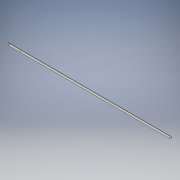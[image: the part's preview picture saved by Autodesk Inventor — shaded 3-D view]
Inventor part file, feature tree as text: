
AUTODESK INVENTOR PART (.ipt)
format: ipt  version: 2017 (Build 210142000, 142)  size: 114,688 bytes
history: native  units: in
note: dims shown in document units (in); Inventor stores cm internally (conversion verified against a paired STEP export)
features: extrude x3, sketch x3
ambient origin geometry x8: Origin, YZ Plane, XZ Plane, XY Plane, X Axis, Y Axis, Z Axis, Center Point
bodies: Solid1 (feature_tree)
feature tree (6):
  extrude  "Extrusion1"  Depth=0.128in
  extrude  "Extrusion2"  Depth=72.0in
  extrude  "Extrusion3"  Depth=72.0in
  sketch  "Sketch1"  dims[d0=1.0in d1=0.128in]
  sketch  "Sketch2"  dims[d2=72.0in d3=0.0in d4=0.25in]
  sketch  "Sketch3"  dims[d5=0.5in d6=5.5in d7=72.0in d8=0.0in d9=0.25in d10=0.5in d11=5.5in d12=72.0in d13=0.0in]
